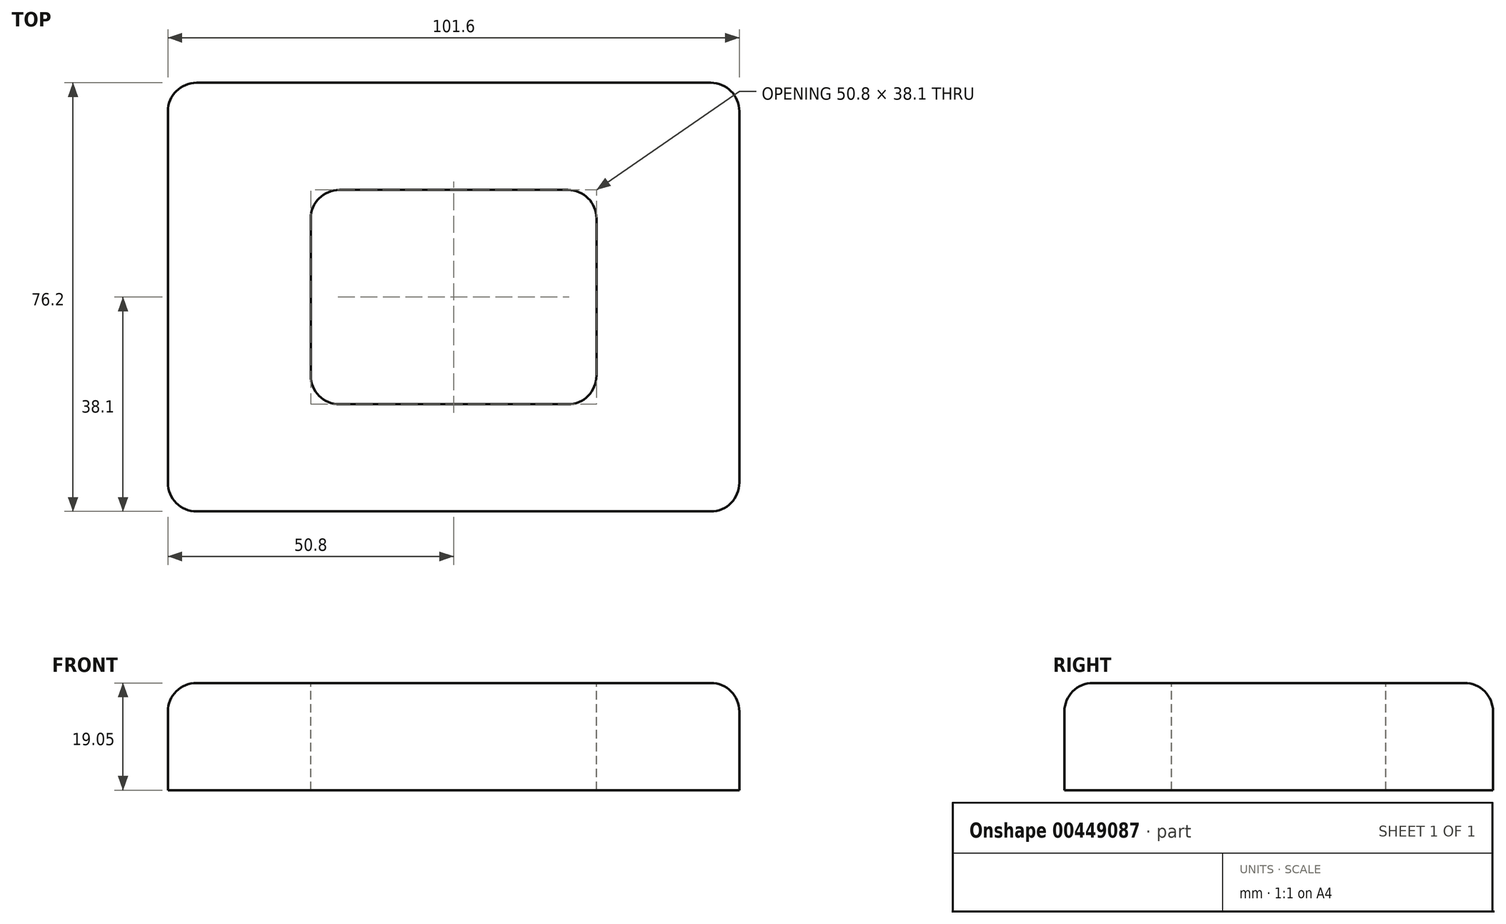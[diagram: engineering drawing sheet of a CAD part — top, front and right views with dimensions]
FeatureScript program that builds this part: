
annotation { "Feature Type Name" : "Feature", "Feature Type Description" : "" }
export const myFeature = defineFeature(function(context is Context, id is Id, definition is map)
    precondition{}
    {
        {
            var Q0;
            Q0=qCreatedBy(makeId("Top.planeOp"),FACE);
            var sketch = newSketch(context, id + "F0", { "sketchPlane" : qUnion([Q0])});
            skLineSegment(sketch, "E0.bottom", {"start": v(50.8, -38.1) * mm, "end": v(-50.8, -38.1) * mm});
            skLineSegment(sketch, "E0.top", {"start": v(50.8, 38.1) * mm, "end": v(-50.8, 38.1) * mm});
            skLineSegment(sketch, "E0.left", {"start": v(50.8, -38.1) * mm, "end": v(50.8, 38.1) * mm});
            skLineSegment(sketch, "E0.right", {"start": v(-50.8, -38.1) * mm, "end": v(-50.8, 38.1) * mm});
            skPoint(sketch, "E0.middle", {"position": v(0, 0) * mm});
            skSolve(sketch);
        }
        {
            var Q0;
            Q0 = qSketchRegion(id + "F0", true);
            extrude(context, id + "F1", {"entities" : qUnion([Q0]), "depth" : 19.05 * mm});
        }
        {
            var Q0;
            Q0=makeQuery(id+"F1.opExtrude","CAP_FACE",FACE,{"disambiguationData":[OSD([sQuery(id+"F0.wireOp",EDGE,"E0.bottom"),sQuery(id+"F0.wireOp",EDGE,"E0.top"),sQuery(id+"F0.wireOp",EDGE,"E0.left"),sQuery(id+"F0.wireOp",EDGE,"E0.right")])],"isStart":false});
            var sketch = newSketch(context, id + "F2", { "sketchPlane" : qUnion([Q0])});
            skLineSegment(sketch, "E1.bottom", {"start": v(25.4, -19.05) * mm, "end": v(-25.4, -19.05) * mm});
            skLineSegment(sketch, "E1.top", {"start": v(25.4, 19.05) * mm, "end": v(-25.4, 19.05) * mm});
            skLineSegment(sketch, "E1.left", {"start": v(25.4, -19.05) * mm, "end": v(25.4, 19.05) * mm});
            skLineSegment(sketch, "E1.right", {"start": v(-25.4, -19.05) * mm, "end": v(-25.4, 19.05) * mm});
            skPoint(sketch, "E1.middle", {"position": v(0, 0) * mm});
            skSolve(sketch);
        }
        {
            var Q0;
            Q0 = qSketchRegion(id + "F2", true);
            extrude(context, id + "F3", {"entities" : qUnion([Q0]), "operationType" : NewBodyOperationType.REMOVE, "oppositeDirection" : true, "depth" : 25.4 * mm});
        }
        {
            var Q0;
            Q0=makeQuery(id+"F1.opExtrude","SWEPT_EDGE",EDGE,{"disambiguationData":[OSD([sQuery(id+"F0.wireOp",EDGE,"E0.top"),sQuery(id+"F0.wireOp",EDGE,"E0.right")])]});
            var Q1;
            Q1=makeQuery(id+"F1.opExtrude","SWEPT_EDGE",EDGE,{"disambiguationData":[OSD([sQuery(id+"F0.wireOp",EDGE,"E0.bottom"),sQuery(id+"F0.wireOp",EDGE,"E0.right")])]});
            var Q2;
            Q2=makeQuery(id+"F1.opExtrude","SWEPT_EDGE",EDGE,{"disambiguationData":[OSD([sQuery(id+"F0.wireOp",EDGE,"E0.top"),sQuery(id+"F0.wireOp",EDGE,"E0.left")])]});
            var Q3;
            Q3=makeQuery(id+"F3.boolean.opBoolean","COPY",EDGE,{"derivedFrom":makeQuery(id+"F3.opExtrude","SWEPT_EDGE",EDGE,{"disambiguationData":[OSD([sQuery(id+"F2.wireOp",EDGE,"E1.bottom"),sQuery(id+"F2.wireOp",EDGE,"E1.left")])]})});
            var Q4;
            Q4=makeQuery(id+"F3.boolean.opBoolean","COPY",EDGE,{"derivedFrom":makeQuery(id+"F3.opExtrude","SWEPT_EDGE",EDGE,{"disambiguationData":[OSD([sQuery(id+"F2.wireOp",EDGE,"E1.top"),sQuery(id+"F2.wireOp",EDGE,"E1.right")])]})});
            var Q5;
            Q5=makeQuery(id+"F1.opExtrude","SWEPT_EDGE",EDGE,{"disambiguationData":[OSD([sQuery(id+"F0.wireOp",EDGE,"E0.bottom"),sQuery(id+"F0.wireOp",EDGE,"E0.left")])]});
            var Q6;
            Q6=makeQuery(id+"F3.boolean.opBoolean","COPY",EDGE,{"derivedFrom":makeQuery(id+"F3.opExtrude","SWEPT_EDGE",EDGE,{"disambiguationData":[OSD([sQuery(id+"F2.wireOp",EDGE,"E1.bottom"),sQuery(id+"F2.wireOp",EDGE,"E1.right")])]})});
            var Q7;
            Q7=makeQuery(id+"F3.boolean.opBoolean","COPY",EDGE,{"derivedFrom":makeQuery(id+"F3.opExtrude","CAP_EDGE",EDGE,{"disambiguationData":[OSD([sQuery(id+"F2.wireOp",EDGE,"E1.right")])],"isStart":true})});
            var Q8;
            Q8=makeQuery(id+"F1.opExtrude","CAP_EDGE",EDGE,{"disambiguationData":[OSD([sQuery(id+"F0.wireOp",EDGE,"E0.right")])],"isStart":false});
            var Q9;
            Q9=makeQuery(id+"F1.opExtrude","CAP_EDGE",EDGE,{"disambiguationData":[OSD([sQuery(id+"F0.wireOp",EDGE,"E0.bottom")])],"isStart":false});
            var Q10;
            Q10=makeQuery(id+"F1.opExtrude","CAP_EDGE",EDGE,{"disambiguationData":[OSD([sQuery(id+"F0.wireOp",EDGE,"E0.left")])],"isStart":false});
            var Q11;
            Q11=makeQuery(id+"F1.opExtrude","CAP_EDGE",EDGE,{"disambiguationData":[OSD([sQuery(id+"F0.wireOp",EDGE,"E0.top")])],"isStart":false});
            var Q12;
            Q12=makeQuery(id+"F3.boolean.opBoolean","COPY",EDGE,{"derivedFrom":makeQuery(id+"F3.opExtrude","SWEPT_EDGE",EDGE,{"disambiguationData":[OSD([sQuery(id+"F2.wireOp",EDGE,"E1.top"),sQuery(id+"F2.wireOp",EDGE,"E1.left")])]})});
            fillet(context, id + "F4", {"entities" : qUnion([Q0, Q1, Q2, Q3, Q4, Q5, Q6, Q7, Q8, Q9, Q10, Q11, Q12]), "radius" : 5.08 * mm, "tangentPropagation" : true, "allowEdgeOverflow" : false});
        }
    });
